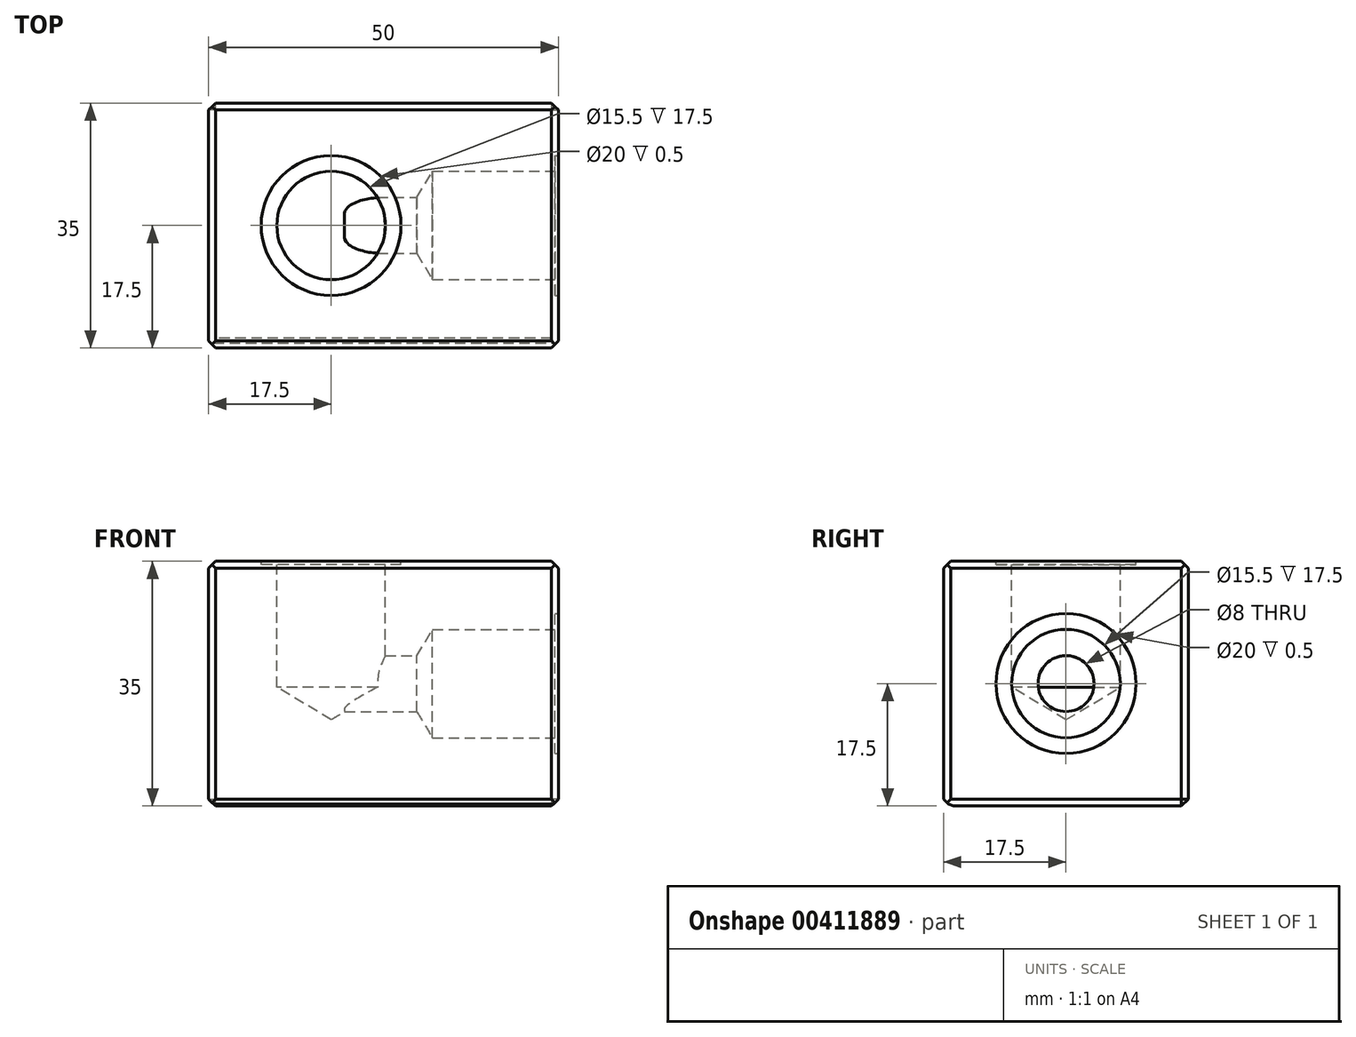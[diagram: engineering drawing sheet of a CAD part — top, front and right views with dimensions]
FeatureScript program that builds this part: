
annotation { "Feature Type Name" : "Feature", "Feature Type Description" : "" }
export const myFeature = defineFeature(function(context is Context, id is Id, definition is map)
    precondition{}
    {
        {
            var Q0;
            Q0=qCreatedBy(makeId("Front.planeOp"),FACE);
            var sketch = newSketch(context, id + "F0", { "sketchPlane" : qUnion([Q0])});
            skLineSegment(sketch, "E0.bottom", {"start": v(0, 0) * mm, "end": v(50, 0) * mm});
            skLineSegment(sketch, "E0.top", {"start": v(0, 35) * mm, "end": v(50, 35) * mm});
            skLineSegment(sketch, "E0.left", {"start": v(0, 0) * mm, "end": v(0, 35) * mm});
            skLineSegment(sketch, "E0.right", {"start": v(50, 0) * mm, "end": v(50, 35) * mm});
            skSolve(sketch);
        }
        {
            var Q0;
            Q0=makeQuery(id+"F0.imprint","IMPRINT",FACE,{"disambiguationData":[TD([[makeQuery(id+"F0.imprint","IMPRINT",EDGE,{"derivedFrom":sQuery(id+"F0.wireOp",EDGE,"E0.bottom")}),1.0]])]});
            extrude(context, id + "F1", {"entities" : qUnion([Q0]), "depth" : 35 * mm});
        }
        {
            var Q0;
            Q0=makeQuery(id+"F1.opExtrude","SWEPT_FACE",FACE,{"disambiguationData":[OSD([sQuery(id+"F0.wireOp",EDGE,"E0.right")])]});
            var sketch = newSketch(context, id + "F2", { "sketchPlane" : qUnion([Q0])});
            skPoint(sketch, "E1", {"position": v(-17.5, 17.5) * mm});
            skSolve(sketch);
        }
        {
            var Q0;
            Q0=sQuery(id+"F2.wireOp",VERTEX,"E1");
            var Q1;
            Q1=makeQuery(id+"F1.opExtrude","SWEPT_BODY",BODY,{"disambiguationData":[OSD([sQuery(id+"F0.wireOp",EDGE,"E0.bottom"),sQuery(id+"F0.wireOp",EDGE,"E0.top"),sQuery(id+"F0.wireOp",EDGE,"E0.left"),sQuery(id+"F0.wireOp",EDGE,"E0.right")])]});
            hole(context, id + "F3", {"style" : HoleStyle.SIMPLE, "endStyle" : HoleEndStyle.BLIND, "standardTappedOrClearance" : lookupTablePath({ "standard" : "ISO", "fit" : "Normal", "size" : "M14", "type" : "Clearance" }), "standardBlindInLast" : lookupTablePath({ "fit" : "Standard", "standard" : "ISO", "size" : "M14", "type" : "Clearance" }), "holeDiameter" : 15.5 * mm, "majorDiameter" : 5 * mm, "holeDepth" : 18 * mm, "isTappedThrough" : true, "tappedDepth" : 12 * mm, "tapClearance" : 3, "locations" : qUnion([Q0]), "scope" : qUnion([Q1])});
        }
        {
            var Q0;
            Q0=makeQuery(id+"F1.opExtrude","SWEPT_FACE",FACE,{"disambiguationData":[OSD([sQuery(id+"F0.wireOp",EDGE,"E0.top")])]});
            var sketch = newSketch(context, id + "F4", { "sketchPlane" : qUnion([Q0])});
            skPoint(sketch, "E2", {"position": v(17.5, -17.5) * mm});
            skSolve(sketch);
        }
        {
            var Q0;
            Q0=sQuery(id+"F4.wireOp",VERTEX,"E2");
            var Q1;
            Q1=makeQuery(id+"F1.opExtrude","SWEPT_BODY",BODY,{"disambiguationData":[OSD([sQuery(id+"F0.wireOp",EDGE,"E0.bottom"),sQuery(id+"F0.wireOp",EDGE,"E0.top"),sQuery(id+"F0.wireOp",EDGE,"E0.left"),sQuery(id+"F0.wireOp",EDGE,"E0.right")])]});
            hole(context, id + "F5", {"style" : HoleStyle.SIMPLE, "endStyle" : HoleEndStyle.BLIND, "standardTappedOrClearance" : lookupTablePath({ "standard" : "ISO", "fit" : "Normal", "size" : "M14", "type" : "Clearance" }), "standardBlindInLast" : lookupTablePath({ "fit" : "Standard", "standard" : "ISO", "size" : "M14", "type" : "Clearance" }), "holeDiameter" : 15.5 * mm, "holeDepth" : 18 * mm, "isTappedThrough" : true, "tappedDepth" : 12 * mm, "tapClearance" : 3, "locations" : qUnion([Q0]), "scope" : qUnion([Q1])});
        }
        {
            var Q0;
            Q0=makeQuery(id+"F1.opExtrude","SWEPT_FACE",FACE,{"disambiguationData":[OSD([sQuery(id+"F0.wireOp",EDGE,"E0.right")])]});
            var sketch = newSketch(context, id + "F6", { "sketchPlane" : qUnion([Q0])});
            skPoint(sketch, "E3", {"position": v(-17.5, 17.5) * mm});
            skSolve(sketch);
        }
        {
            var Q0;
            Q0=sQuery(id+"F6.wireOp",VERTEX,"E3");
            var Q1;
            Q1=makeQuery(id+"F1.opExtrude","SWEPT_BODY",BODY,{"disambiguationData":[OSD([sQuery(id+"F0.wireOp",EDGE,"E0.bottom"),sQuery(id+"F0.wireOp",EDGE,"E0.top"),sQuery(id+"F0.wireOp",EDGE,"E0.left"),sQuery(id+"F0.wireOp",EDGE,"E0.right")])]});
            hole(context, id + "F7", {"style" : HoleStyle.SIMPLE, "endStyle" : HoleEndStyle.BLIND, "holeDiameter" : 8 * mm, "holeDepth" : 33 * mm, "isTappedThrough" : true, "tappedDepth" : 12 * mm, "tapClearance" : 3, "startFromSketch" : true, "locations" : qUnion([Q0]), "scope" : qUnion([Q1])});
        }
        {
            var Q0;
            Q0=makeQuery(id+"F1.opExtrude","SWEPT_FACE",FACE,{"disambiguationData":[OSD([sQuery(id+"F0.wireOp",EDGE,"E0.right")])]});
            var sketch = newSketch(context, id + "F8", { "sketchPlane" : qUnion([Q0])});
            skCircle(sketch, "E4", {"center": v(-17.5, 17.5) * mm, "radius": 10 * mm});
            skSolve(sketch);
        }
        {
            var Q0;
            Q0=makeQuery(id+"F8.imprint","IMPRINT",FACE,{"disambiguationData":[TD([[makeQuery(id+"F8.imprint","IMPRINT",EDGE,{"derivedFrom":sQuery(id+"F8.wireOp",EDGE,"E4")}),1.0]])]});
            extrude(context, id + "F9", {"entities" : qUnion([Q0]), "operationType" : NewBodyOperationType.REMOVE, "oppositeDirection" : true, "depth" : .5 * mm});
        }
        {
            var Q0;
            Q0=makeQuery(id+"F1.opExtrude","SWEPT_FACE",FACE,{"disambiguationData":[OSD([sQuery(id+"F0.wireOp",EDGE,"E0.top")])]});
            var sketch = newSketch(context, id + "F10", { "sketchPlane" : qUnion([Q0])});
            skCircle(sketch, "E5", {"center": v(17.5, -17.5) * mm, "radius": 10 * mm});
            skSolve(sketch);
        }
        {
            var Q0;
            Q0=makeQuery(id+"F10.imprint","IMPRINT",FACE,{"disambiguationData":[TD([[makeQuery(id+"F10.imprint","IMPRINT",EDGE,{"derivedFrom":sQuery(id+"F10.wireOp",EDGE,"E5")}),1.0]])]});
            extrude(context, id + "F11", {"entities" : qUnion([Q0]), "operationType" : NewBodyOperationType.REMOVE, "oppositeDirection" : true, "depth" : .5 * mm});
        }
        {
            var Q0;
            Q0=makeQuery(id+"F1.opExtrude","CAP_FACE",FACE,{"disambiguationData":[OSD([sQuery(id+"F0.wireOp",EDGE,"E0.bottom"),sQuery(id+"F0.wireOp",EDGE,"E0.top"),sQuery(id+"F0.wireOp",EDGE,"E0.left"),sQuery(id+"F0.wireOp",EDGE,"E0.right")])],"isStart":false});
            chamfer(context, id + "F12", {"entities" : qUnion([Q0]), "width" : 1 * mm, "tangentPropagation" : true});
        }
        {
            var Q0;
            Q0=makeQuery(id+"F1.opExtrude","CAP_FACE",FACE,{"disambiguationData":[OSD([sQuery(id+"F0.wireOp",EDGE,"E0.bottom"),sQuery(id+"F0.wireOp",EDGE,"E0.top"),sQuery(id+"F0.wireOp",EDGE,"E0.left"),sQuery(id+"F0.wireOp",EDGE,"E0.right")])],"isStart":true});
            var Q1;
            Q1=makeQuery(id+"F1.opExtrude","SWEPT_FACE",FACE,{"disambiguationData":[OSD([sQuery(id+"F0.wireOp",EDGE,"E0.bottom")])]});
            chamfer(context, id + "F13", {"entities" : qUnion([Q0, Q1]), "width" : 1 * mm, "tangentPropagation" : true});
        }
        {
            var Q0;
            Q0=makeQuery(id+"F1.opExtrude","SWEPT_EDGE",EDGE,{"disambiguationData":[OSD([sQuery(id+"F0.wireOp",EDGE,"E0.top"),sQuery(id+"F0.wireOp",EDGE,"E0.left")])]});
            var Q1;
            Q1=makeQuery(id+"F1.opExtrude","SWEPT_EDGE",EDGE,{"disambiguationData":[OSD([sQuery(id+"F0.wireOp",EDGE,"E0.top"),sQuery(id+"F0.wireOp",EDGE,"E0.right")])]});
            chamfer(context, id + "F14", {"entities" : qUnion([Q0, Q1]), "width" : 1 * mm, "tangentPropagation" : true});
        }
    });
